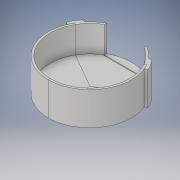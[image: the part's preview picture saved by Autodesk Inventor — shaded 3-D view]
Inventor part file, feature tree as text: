
AUTODESK INVENTOR PART (.ipt)
format: ipt  version: 2019 (Build 230136000, 136)  size: 546,304 bytes
history: native  units: mm
features: sketch x7, extrude x6, plane x5, fillet x4, split x3, loft x2, other x2, boolean_combine x1
ambient origin geometry x8: Origin, YZ Plane, XZ Plane, XY Plane, X Axis, Y Axis, Z Axis, Center Point
bodies: Solid1 (feature_tree), Solid2 (feature_tree), Solid3 (feature_tree), Solid4 (feature_tree), Solid5 (feature_tree), Solid6 (feature_tree), Solid7 (feature_tree)
feature tree (30):
  extrude  "Extrusion1"  Depth=126.0mm
  extrude  "Extrusion2"  Depth=40.0mm
  extrude  "Extrusion3"  Depth=60.0mm
  plane  "Work Plane2"
  plane  "Work Plane3"
  extrude  "Extrusion6"  Depth=10.0mm TaperAngle=0.0deg
  loft  "Loft3"
  extrude  "Extrusion7"  Depth=20.0mm TaperAngle=0.0deg
  loft  "Loft4"
  fillet  "Fillet5"  [1 undecoded]
  fillet  "Fillet6"  [1 undecoded]
  fillet  "Fillet7"  [1 undecoded]
  fillet  "Fillet8"  Radius=20.0mm
  plane  "Work Plane6"
  split  "Split1"
  split  "Split2"
  split  "Split3"
  boolean_combine  "Combine1"
  extrude  "Extrusion8"  TaperAngle=0.0deg  [1 undecoded]
  sketch  "Sketch1"  dims[d0=120.0mm d1=126.0mm]
  sketch  "Sketch2"  dims[d2=40.0mm d3=0.0mm d4=1.0mm]
  sketch  "Sketch3"  dims[d5=1.0mm d6=60.0mm]
  sketch  "Sketch11"  dims[d7=120.0mm d8=10.0mm d9=0.0mm]
  sketch  "Sketch12"  dims[d10=10.0mm d11=0.0mm d21=40.0mm]
  sketch  "Sketch13"  dims[d27=20.0mm d28=20.0mm d29=0.0mm]
  other  "Edges3"
  other  "Edges4"
  plane  "Work Plane4"
  plane  "Work Plane5"
  sketch  "Sketch14"  dims[d36=126.0mm d37=126.0mm d43=120.0deg d45=0.0mm d46=90.0deg d47=0.0mm d48=90.0deg d49=20.0mm d50=0.0mm d51=0.0mm d52=90.0deg d53=0.0mm d54=90.0deg d56=4.0mm d57=4.0mm d58=4.0mm d59=4.0mm d60=20.0mm d61=0.0mm]
note: 4 required parameter values undecoded (feature->parameter linkage not recoverable at this tier; creation-order binding heuristic only, values carry confidence <= 0.55)
